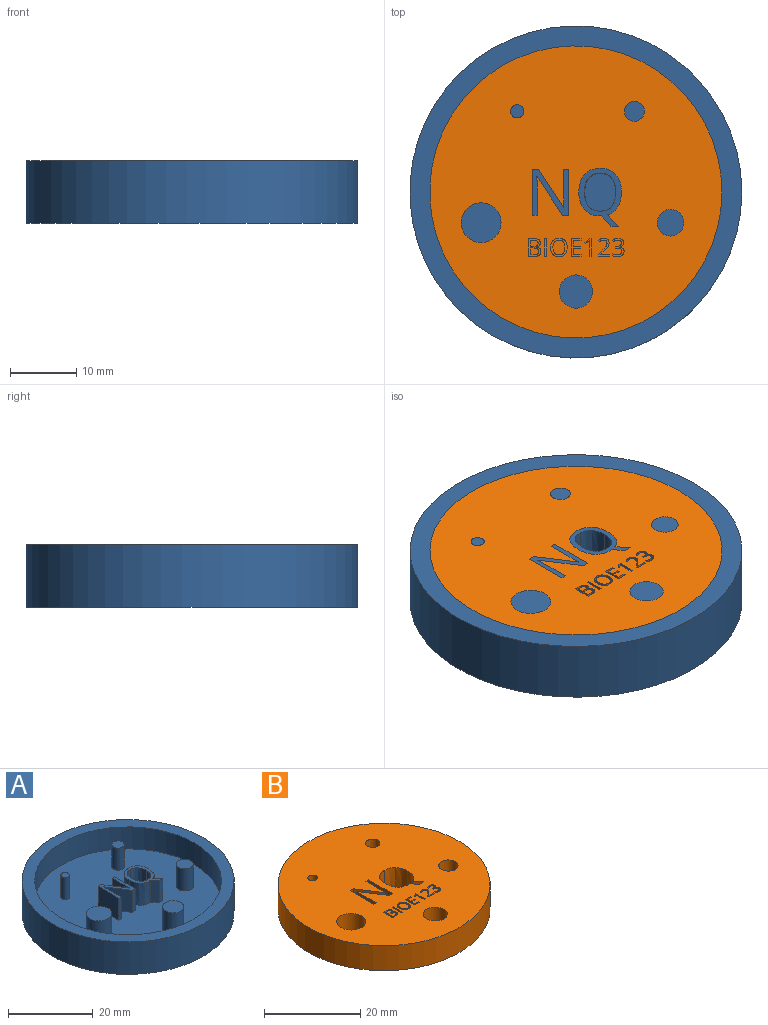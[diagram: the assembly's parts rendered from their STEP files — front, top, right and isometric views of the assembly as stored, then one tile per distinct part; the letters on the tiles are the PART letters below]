
ASSEMBLY  parts=2 mates=1
PART A: 53 faces, bbox 50x50x9.4 mm
  f0: cylinder r=25mm len=50mm, axis (0,0,-1), area 1468.7mm2, adj f1,f3
  f1: plane 50x50mm, normal (0,0,-1), area 1963.5mm2, adj f0
  f2: cylinder r=22mm len=44mm, axis (0,0,-1), area 877.8mm2, adj f3,f4
  f3: plane 50x50mm, normal (0,0,1), area 443mm2, adj f0,f2
  f4: plane 44x44mm, normal (0,0,1), area 1394.3mm2, adj f2,f5,f7,f9,f11,f13,f15,f16
  f5: cylinder r=1mm len=6.35mm, axis (0,0,-1), area 39.9mm2, adj f4,f6
  f6: plane 2x2mm, normal (0,0,1), area 3.1mm2, adj f5
  f7: cylinder r=1.5mm len=6.35mm, axis (0,0,-1), area 59.8mm2, adj f4,f8
  f8: plane 3x3mm, normal (0,0,1), area 7.1mm2, adj f7
  f9: cylinder r=3mm len=6.35mm, axis (0,0,-1), area 119.7mm2, adj f4,f10
  f10: plane 6x6mm, normal (0,0,1), area 28.3mm2, adj f9
  f11: cylinder r=2mm len=6.35mm, axis (0,0,-1), area 79.8mm2, adj f4,f12
  f12: plane 4x4mm, normal (0,0,1), area 12.6mm2, adj f11
  f13: cylinder r=2.5mm len=6.35mm, axis (0,0,-1), area 99.7mm2, adj f4,f14
  f14: plane 5x5mm, normal (0,0,1), area 19.6mm2, adj f13
  f15: plane 6.97x6.35mm, normal (1,0,0), area 44.3mm2, adj f4,f16,f29,f30
  f16: plane 6.35x0.76mm, normal (0,1,0), area 4.8mm2, adj f4,f15,f17,f30
  f17: plane 6.35x4mm, normal (-1,0,0), area 25.4mm2, adj f4,f16,f18,f30
  f18: extruded ~6.35x1mm, area 6.3mm2, adj f4,f17,f19,f30
  f19: extruded ~6.35x0.83mm, area 5.3mm2, adj f4,f18,f20,f30
  f20: plane 6.35x0.04mm, normal (0,1,0), area 0.2mm2, adj f4,f19,f21,f30
  f21: plane 6.35x5.83mm, normal (0.84,0.55,0), area 44.2mm2, adj f4,f20,f22,f30
  f22: plane 6.35x0.92mm, normal (0,1,0), area 5.8mm2, adj f4,f21,f23,f30
  f23: plane 6.97x6.35mm, normal (-1,0,0), area 44.3mm2, adj f4,f22,f24,f30
  f24: plane 6.35x0.75mm, normal (0,-1,0), area 4.8mm2, adj f4,f23,f25,f30
  f25: plane 6.35x3.96mm, normal (1,0,0), area 25.2mm2, adj f4,f24,f26,f30
  f26: extruded ~6.35x1.89mm, area 12mm2, adj f4,f25,f27,f30
  f27: plane 6.35x0.04mm, normal (0,-1,0), area 0.2mm2, adj f4,f26,f28,f30
  f28: plane 6.35x5.85mm, normal (-0.84,-0.55,0), area 44.3mm2, adj f4,f27,f29,f30
  f29: plane 6.35x0.92mm, normal (0,-1,0), area 5.9mm2, adj f4,f15,f28,f30
  f30: plane 6.97x5.44mm, normal (0,0,1), area 16mm2, adj f15,f16,f17,f18,f19,f20,f21,f22
  f31: extruded ~6.35x2.63mm, area 17.9mm2, adj f4,f32,f50,f51
  f32: extruded ~6.35x2.35mm, area 16.6mm2, adj f4,f31,f33,f51
  f33: extruded ~6.35x2.38mm, area 16.8mm2, adj f4,f32,f34,f51
  f34: extruded ~6.35x2.64mm, area 18mm2, adj f4,f33,f35,f51
  f35: extruded ~6.35x2.66mm, area 18.1mm2, adj f4,f34,f36,f51
  f36: extruded ~6.35x2.38mm, area 16.8mm2, adj f4,f35,f37,f51
  f37: plane 6.35x0.26mm, normal (0.04,-1,0), area 1.7mm2, adj f4,f36,f38,f51
  f38: plane 6.35x1.57mm, normal (-0.76,-0.65,0), area 13.2mm2, adj f4,f37,f39,f51
  f39: plane 6.35x1.18mm, normal (0,-1,0), area 7.5mm2, adj f4,f38,f40,f51
  f40: plane 6.35x1.73mm, normal (0.72,0.69,0), area 15.2mm2, adj f4,f39,f41,f51
  f41: extruded ~6.35x1.52mm, area 12.6mm2, adj f4,f40,f50,f51
  f42: extruded ~6.35x2.13mm, area 14.3mm2, adj f43,f49,f51,f52
  f43: extruded ~6.35x1.76mm, area 12.5mm2, adj f42,f44,f51,f52
  f44: extruded ~6.35x1.74mm, area 12.4mm2, adj f43,f45,f51,f52
  f45: extruded ~6.35x2.13mm, area 14.3mm2, adj f44,f46,f51,f52
  f46: extruded ~6.35x2.15mm, area 14.4mm2, adj f45,f47,f51,f52
  f47: extruded ~6.35x1.75mm, area 12.5mm2, adj f46,f48,f51,f52
  f48: extruded ~6.35x1.75mm, area 12.5mm2, adj f47,f49,f51,f52
  f49: extruded ~6.35x2.15mm, area 14.4mm2, adj f42,f48,f51,f52
  f50: extruded ~6.35x2.23mm, area 14.7mm2, adj f4,f31,f41,f51
  f51: plane 8.74x6.41mm, normal (0,0,1), area 17.2mm2, adj f31,f32,f33,f34,f35,f36,f37,f38
  f52: plane 5.74x4.7mm, normal (0,0,1), area 22.3mm2, adj f42,f43,f44,f45,f46,f47,f48,f49
PART B: 159 faces, bbox 44x44x6.4 mm
  f0: plane 44x44mm, normal (0,0,1), area 1377.3mm2, adj f1,f2,f3,f4,f5,f6,f7,f8
  f1: extruded ~6.35x2.35mm, area 16.6mm2, adj f0,f2,f33,f34
  f2: extruded ~6.35x2.63mm, area 17.9mm2, adj f0,f1,f3,f34
  f3: extruded ~6.35x2.23mm, area 14.7mm2, adj f0,f2,f4,f34
  f4: extruded ~6.35x1.52mm, area 12.6mm2, adj f0,f3,f5,f34
  f5: plane 6.35x1.73mm, normal (-0.72,-0.69,0), area 15.2mm2, adj f0,f4,f6,f34
  f6: plane 6.35x1.18mm, normal (0,1,0), area 7.5mm2, adj f0,f5,f7,f34
  f7: plane 6.35x1.57mm, normal (0.76,0.65,0), area 13.2mm2, adj f0,f6,f8,f34
  f8: plane 6.35x0.26mm, normal (-0.04,1,0), area 1.7mm2, adj f0,f7,f9,f34
  f9: extruded ~6.35x2.38mm, area 16.8mm2, adj f0,f8,f10,f34
  f10: extruded ~6.35x2.66mm, area 18.1mm2, adj f0,f9,f11,f34
  f11: extruded ~6.35x2.64mm, area 18mm2, adj f0,f10,f33,f34
  f12: plane 6.35x0.76mm, normal (0,-1,0), area 4.8mm2, adj f0,f13,f26,f34
  f13: plane 6.97x6.35mm, normal (-1,0,0), area 44.3mm2, adj f0,f12,f14,f34
  f14: plane 6.35x0.92mm, normal (0,1,0), area 5.9mm2, adj f0,f13,f15,f34
  f15: plane 6.35x5.85mm, normal (0.84,0.55,0), area 44.3mm2, adj f0,f14,f16,f34
  f16: plane 6.35x0.04mm, normal (0,1,0), area 0.2mm2, adj f0,f15,f17,f34
  f17: extruded ~6.35x1.89mm, area 12mm2, adj f0,f16,f18,f34
  f18: plane 6.35x3.96mm, normal (-1,0,0), area 25.2mm2, adj f0,f17,f19,f34
  f19: plane 6.35x0.75mm, normal (0,1,0), area 4.8mm2, adj f0,f18,f20,f34
  f20: plane 6.97x6.35mm, normal (1,0,0), area 44.3mm2, adj f0,f19,f21,f34
  f21: plane 6.35x0.92mm, normal (0,-1,0), area 5.8mm2, adj f0,f20,f22,f34
  f22: plane 6.35x5.83mm, normal (-0.84,-0.55,0), area 44.2mm2, adj f0,f21,f23,f34
  f23: plane 6.35x0.04mm, normal (0,-1,0), area 0.2mm2, adj f0,f22,f24,f34
  f24: extruded ~6.35x0.83mm, area 5.3mm2, adj f0,f23,f25,f34
  f25: extruded ~6.35x1mm, area 6.3mm2, adj f0,f24,f26,f34
  f26: plane 6.35x4mm, normal (1,0,0), area 25.4mm2, adj f0,f12,f25,f34
  f27: cylinder r=22mm len=44mm, axis (0,0,-1), area 877.8mm2, adj f0,f34
  f28: cylinder r=3mm len=6.35mm, axis (0,0,-1), area 119.7mm2, adj f0,f34
  f29: cylinder r=2.5mm len=6.35mm, axis (0,0,-1), area 99.7mm2, adj f0,f34
  f30: cylinder r=2mm len=6.35mm, axis (0,0,-1), area 79.8mm2, adj f0,f34
  f31: cylinder r=1.5mm len=6.35mm, axis (0,0,-1), area 59.8mm2, adj f0,f34
  f32: cylinder r=1mm len=6.35mm, axis (0,0,-1), area 39.9mm2, adj f0,f34
  f33: extruded ~6.35x2.38mm, area 16.8mm2, adj f0,f1,f11,f34
  f34: plane 44x44mm, normal (0,0,-1), area 1394.3mm2, adj f1,f2,f3,f4,f5,f6,f7,f8
  f35: plane 0.5x0.31mm, normal (0,1,0), area 0.2mm2, adj f0,f36,f38,f39
  f36: plane 2.69x0.5mm, normal (-1,0,0), area 1.3mm2, adj f0,f35,f37,f39
  f37: plane 0.5x0.31mm, normal (0,-1,0), area 0.2mm2, adj f0,f36,f38,f39
  f38: plane 2.69x0.5mm, normal (1,0,0), area 1.3mm2, adj f0,f35,f37,f39
  f39: plane 2.69x0.31mm, normal (0,0,1), area 0.8mm2, adj f35,f36,f37,f38
  f40: plane 0.5x0.28mm, normal (-1,0,0), area 0.1mm2, adj f0,f41,f51,f52
  f41: plane 1.19x0.5mm, normal (0,-1,0), area 0.6mm2, adj f0,f40,f42,f52
  f42: plane 0.99x0.5mm, normal (-1,0,0), area 0.5mm2, adj f0,f41,f43,f52
  f43: plane 1.11x0.5mm, normal (0,1,0), area 0.6mm2, adj f0,f42,f44,f52
  f44: plane 0.5x0.28mm, normal (-1,0,0), area 0.1mm2, adj f0,f43,f45,f52
  f45: plane 1.11x0.5mm, normal (0,-1,0), area 0.6mm2, adj f0,f44,f46,f52
  f46: plane 0.87x0.5mm, normal (-1,0,0), area 0.4mm2, adj f0,f45,f47,f52
  f47: plane 1.19x0.5mm, normal (0,1,0), area 0.6mm2, adj f0,f46,f48,f52
  f48: plane 0.5x0.28mm, normal (-1,0,0), area 0.1mm2, adj f0,f47,f49,f52
  f49: plane 1.5x0.5mm, normal (0,-1,0), area 0.7mm2, adj f0,f48,f50,f52
  f50: plane 2.69x0.5mm, normal (1,0,0), area 1.3mm2, adj f0,f49,f51,f52
  f51: plane 1.5x0.5mm, normal (0,1,0), area 0.7mm2, adj f0,f40,f50,f52
  f52: plane 2.69x1.5mm, normal (0,0,1), area 1.8mm2, adj f40,f41,f42,f43,f44,f45,f46,f47
  f53: plane 2.69x0.5mm, normal (-1,0,0), area 1.3mm2, adj f0,f54,f61,f62
  f54: plane 0.5x0.26mm, normal (0,-1,0), area 0.1mm2, adj f0,f53,f55,f62
  f55: plane 0.71x0.55mm, normal (0.61,-0.79,0), area 0.4mm2, adj f0,f54,f56,f62
  f56: plane 0.5x0.21mm, normal (0.79,0.61,0), area 0.1mm2, adj f0,f55,f57,f62
  f57: extruded ~0.5x0.44mm, area 0.3mm2, adj f0,f56,f58,f62
  f58: extruded ~0.5x0.09mm, area 0.1mm2, adj f0,f57,f59,f62
  f59: extruded ~0.5x0.45mm, area 0.2mm2, adj f0,f58,f60,f62
  f60: plane 1.92x0.5mm, normal (1,0,0), area 1mm2, adj f0,f59,f61,f62
  f61: plane 0.5x0.3mm, normal (0,1,0), area 0.1mm2, adj f0,f53,f60,f62
  f62: plane 2.69x0.97mm, normal (0,0,1), area 1mm2, adj f53,f54,f55,f56,f57,f58,f59,f60
  f63: plane 0.5x0.28mm, normal (-1,0,0), area 0.1mm2, adj f0,f64,f82,f83
  f64: plane 1.38x0.5mm, normal (0,-1,0), area 0.7mm2, adj f0,f63,f65,f83
  f65: plane 0.5x0.01mm, normal (-1,0,0), area 0mm2, adj f0,f64,f66,f83
  f66: plane 0.59x0.58mm, normal (-0.7,0.71,0), area 0.4mm2, adj f0,f65,f67,f83
  f67: extruded ~0.63x0.54mm, area 0.4mm2, adj f0,f66,f68,f83
  f68: extruded ~0.51x0.5mm, area 0.3mm2, adj f0,f67,f69,f83
  f69: extruded ~0.52x0.5mm, area 0.3mm2, adj f0,f68,f70,f83
  f70: extruded ~0.59x0.5mm, area 0.3mm2, adj f0,f69,f71,f83
  f71: extruded ~0.81x0.5mm, area 0.4mm2, adj f0,f70,f72,f83
  f72: plane 0.5x0.21mm, normal (0.79,0.61,0), area 0.1mm2, adj f0,f71,f73,f83
  f73: extruded ~0.5x0.33mm, area 0.2mm2, adj f0,f72,f74,f83
  f74: extruded ~0.5x0.32mm, area 0.2mm2, adj f0,f73,f75,f83
  f75: extruded ~0.5x0.36mm, area 0.2mm2, adj f0,f74,f76,f83
  f76: extruded ~0.5x0.34mm, area 0.2mm2, adj f0,f75,f77,f83
  f77: extruded ~0.5x0.29mm, area 0.1mm2, adj f0,f76,f78,f83
  f78: extruded ~0.5x0.27mm, area 0.2mm2, adj f0,f77,f79,f83
  f79: extruded ~0.5x0.47mm, area 0.3mm2, adj f0,f78,f80,f83
  f80: plane 0.71x0.71mm, normal (0.71,-0.71,0), area 0.5mm2, adj f0,f79,f81,f83
  f81: plane 0.5x0.26mm, normal (1,0,0), area 0.1mm2, adj f0,f80,f82,f83
  f82: plane 1.77x0.5mm, normal (0,1,0), area 0.9mm2, adj f0,f63,f81,f83
  f83: plane 2.73x1.77mm, normal (0,0,1), area 1.6mm2, adj f63,f64,f65,f66,f67,f68,f69,f70
  f84: extruded ~0.5x0.49mm, area 0.3mm2, adj f0,f85,f111,f112
  f85: extruded ~0.61x0.5mm, area 0.3mm2, adj f0,f84,f86,f112
  f86: extruded ~0.5x0.46mm, area 0.2mm2, adj f0,f85,f87,f112
  f87: extruded ~0.5x0.38mm, area 0.2mm2, adj f0,f86,f88,f112
  f88: plane 0.5x0.21mm, normal (0.8,0.6,0), area 0.1mm2, adj f0,f87,f89,f112
  f89: extruded ~0.5x0.36mm, area 0.2mm2, adj f0,f88,f90,f112
  f90: extruded ~0.5x0.33mm, area 0.2mm2, adj f0,f89,f91,f112
  f91: extruded ~0.5x0.37mm, area 0.2mm2, adj f0,f90,f92,f112
  f92: extruded ~0.5x0.31mm, area 0.2mm2, adj f0,f91,f93,f112
  f93: extruded ~0.5x0.39mm, area 0.2mm2, adj f0,f92,f94,f112
  f94: extruded ~0.5x0.5mm, area 0.3mm2, adj f0,f93,f95,f112
  f95: plane 0.5x0.27mm, normal (0,-1,0), area 0.1mm2, adj f0,f94,f96,f112
  f96: plane 0.5x0.26mm, normal (1,0,0), area 0.1mm2, adj f0,f95,f97,f112
  f97: plane 0.5x0.27mm, normal (0,1,0), area 0.1mm2, adj f0,f96,f98,f112
  f98: extruded ~0.77x0.5mm, area 0.5mm2, adj f0,f97,f99,f112
  f99: extruded ~0.7x0.55mm, area 0.5mm2, adj f0,f98,f100,f112
  f100: extruded ~0.5x0.37mm, area 0.2mm2, adj f0,f99,f101,f112
  f101: extruded ~0.5x0.37mm, area 0.2mm2, adj f0,f100,f102,f112
  f102: plane 0.5x0.29mm, normal (1,0,0), area 0.1mm2, adj f0,f101,f103,f112
  f103: extruded ~0.5x0.34mm, area 0.2mm2, adj f0,f102,f104,f112
  f104: extruded ~0.5x0.39mm, area 0.2mm2, adj f0,f103,f105,f112
  f105: extruded ~0.76x0.5mm, area 0.4mm2, adj f0,f104,f106,f112
  f106: extruded ~0.59x0.5mm, area 0.3mm2, adj f0,f105,f107,f112
  f107: extruded ~0.5x0.43mm, area 0.2mm2, adj f0,f106,f108,f112
  f108: extruded ~0.5x0.48mm, area 0.3mm2, adj f0,f107,f109,f112
  f109: plane 0.5x0.01mm, normal (-1,0,0), area 0mm2, adj f0,f108,f110,f112
  f110: extruded ~0.5x0.41mm, area 0.2mm2, adj f0,f109,f111,f112
  f111: extruded ~0.5x0.42mm, area 0.2mm2, adj f0,f84,f110,f112
  f112: plane 2.76x1.76mm, normal (0,0,1), area 1.7mm2, adj f84,f85,f86,f87,f88,f89,f90,f91
  f113: extruded ~1.02x0.5mm, area 0.5mm2, adj f0,f114,f128,f129
  f114: extruded ~0.91x0.5mm, area 0.5mm2, adj f0,f113,f115,f129
  f115: extruded ~0.92x0.5mm, area 0.5mm2, adj f0,f114,f116,f129
  f116: extruded ~1.02x0.5mm, area 0.5mm2, adj f0,f115,f117,f129
  f117: extruded ~1.03x0.5mm, area 0.5mm2, adj f0,f116,f118,f129
  f118: extruded ~0.92x0.5mm, area 0.5mm2, adj f0,f117,f119,f129
  f119: extruded ~0.91x0.5mm, area 0.5mm2, adj f0,f118,f128,f129
  f120: extruded ~0.82x0.5mm, area 0.4mm2, adj f121,f127,f129,f130
  f121: extruded ~0.68x0.5mm, area 0.4mm2, adj f120,f122,f129,f130
  f122: extruded ~0.67x0.5mm, area 0.4mm2, adj f121,f123,f129,f130
  f123: extruded ~0.82x0.5mm, area 0.4mm2, adj f122,f124,f129,f130
  f124: extruded ~0.83x0.5mm, area 0.4mm2, adj f123,f125,f129,f130
  f125: extruded ~0.67x0.5mm, area 0.4mm2, adj f124,f126,f129,f130
  f126: extruded ~0.68x0.5mm, area 0.4mm2, adj f125,f127,f129,f130
  f127: extruded ~0.83x0.5mm, area 0.4mm2, adj f120,f126,f129,f130
  f128: extruded ~1.02x0.5mm, area 0.5mm2, adj f0,f113,f119,f129
  f129: plane 2.77x2.47mm, normal (0,0,1), area 2.3mm2, adj f113,f114,f115,f116,f117,f118,f119,f120
  f130: plane 2.21x1.81mm, normal (0,0,1), area 3.3mm2, adj f120,f121,f122,f123,f124,f125,f126,f127
  f131: plane 2.69x0.5mm, normal (1,0,0), area 1.3mm2, adj f0,f132,f155,f156
  f132: plane 0.94x0.5mm, normal (0,1,0), area 0.5mm2, adj f0,f131,f133,f156
  f133: extruded ~0.68x0.5mm, area 0.4mm2, adj f0,f132,f134,f156
  f134: extruded ~0.56x0.5mm, area 0.3mm2, adj f0,f133,f135,f156
  f135: extruded ~0.64x0.61mm, area 0.5mm2, adj f0,f134,f136,f156
  f136: plane 0.5x0.02mm, normal (-1,0,0), area 0mm2, adj f0,f135,f137,f156
  f137: extruded ~0.5x0.39mm, area 0.2mm2, adj f0,f136,f138,f156
  f138: extruded ~0.5x0.4mm, area 0.2mm2, adj f0,f137,f139,f156
  f139: extruded ~0.51x0.5mm, area 0.3mm2, adj f0,f138,f140,f156
  f140: extruded ~0.77x0.5mm, area 0.4mm2, adj f0,f139,f155,f156
  f141: plane 0.88x0.5mm, normal (-1,0,0), area 0.4mm2, adj f142,f153,f156,f158
  f142: plane 0.5x0.46mm, normal (0,1,0), area 0.2mm2, adj f141,f143,f156,f158
  f143: extruded ~0.52x0.5mm, area 0.3mm2, adj f142,f144,f156,f158
  f144: extruded ~0.5x0.33mm, area 0.2mm2, adj f143,f145,f156,f158
  f145: extruded ~0.5x0.35mm, area 0.2mm2, adj f144,f146,f156,f158
  f146: extruded ~0.5x0.48mm, area 0.2mm2, adj f145,f153,f156,f158
  f147: plane 0.54x0.5mm, normal (0,1,0), area 0.3mm2, adj f148,f154,f156,f157
  f148: extruded ~0.51x0.5mm, area 0.3mm2, adj f147,f149,f156,f157
  f149: extruded ~0.5x0.37mm, area 0.2mm2, adj f148,f150,f156,f157
  f150: extruded ~0.5x0.4mm, area 0.2mm2, adj f149,f151,f156,f157
  f151: extruded ~0.5x0.49mm, area 0.3mm2, adj f150,f152,f156,f157
  f152: plane 0.56x0.5mm, normal (0,-1,0), area 0.3mm2, adj f151,f154,f156,f157
  f153: plane 0.52x0.5mm, normal (0,-1,0), area 0.3mm2, adj f141,f146,f156,f158
  f154: plane 1.01x0.5mm, normal (-1,0,0), area 0.5mm2, adj f147,f152,f156,f157
  f155: plane 0.76x0.5mm, normal (0,-1,0), area 0.4mm2, adj f0,f131,f140,f156
  f156: plane 2.69x1.86mm, normal (0,0,1), area 2.5mm2, adj f131,f132,f133,f134,f135,f136,f137,f138
  f157: plane 1.22x1.01mm, normal (0,0,1), area 1.1mm2, adj f147,f148,f149,f150,f151,f152,f154
  f158: plane 1.14x0.88mm, normal (0,0,1), area 0.9mm2, adj f141,f142,f143,f144,f145,f146,f153
PLACE A rot(axis=(-0.7,-0.71,-0.01),0deg) t=(-3.7,-1.82,0.91)mm
PLACE B rot(axis=(-0.7,-0.71,-0.01),0deg) t=(-3.7,-1.82,0.91)mm
MATE fastened B.f28 <-> A.f9  axis (0,0,-1) through (-17.96,-6.46,3.91)mm
